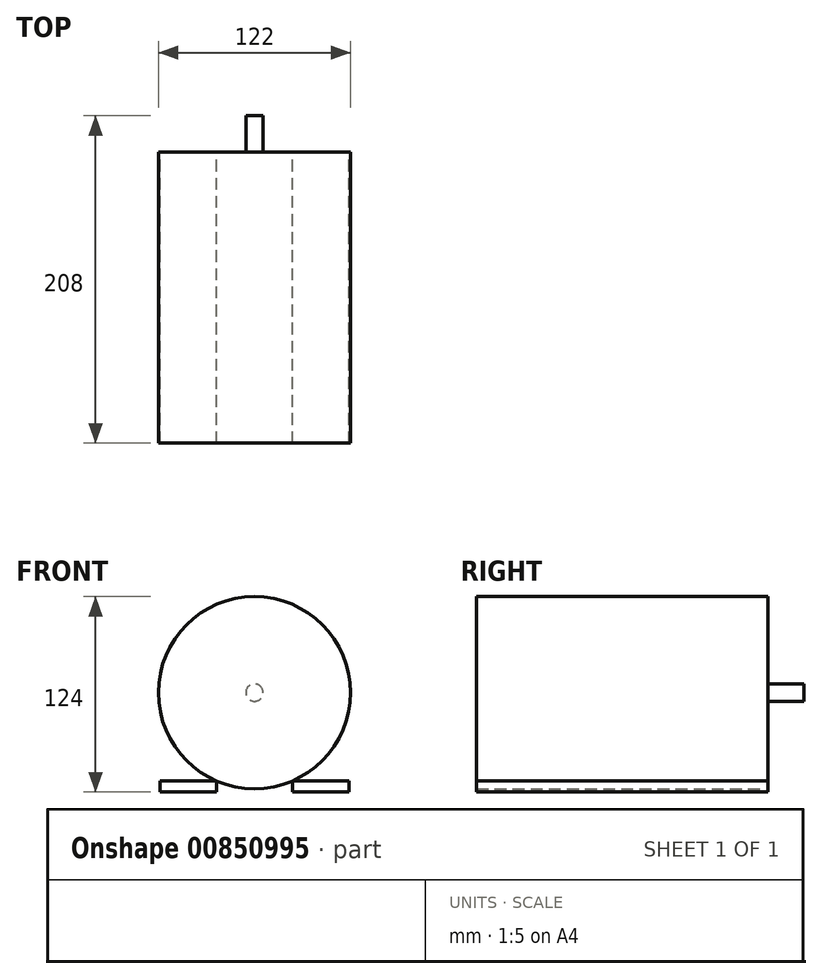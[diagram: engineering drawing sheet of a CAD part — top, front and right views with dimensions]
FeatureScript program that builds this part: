
annotation { "Feature Type Name" : "Feature", "Feature Type Description" : "" }
export const myFeature = defineFeature(function(context is Context, id is Id, definition is map)
    precondition{}
    {
        {
            var Q0;
            Q0=qCreatedBy(makeId("Front.planeOp"),FACE);
            var sketch = newSketch(context, id + "F0", { "sketchPlane" : qUnion([Q0])});
            skCircle(sketch, "E0", {"center": v(0, 0) * mm, "radius": 61 * mm});
            skLineSegment(sketch, "E1.bottom", {"start": v(-24.19, -56) * mm, "end": v(-60, -56) * mm});
            skLineSegment(sketch, "E1.top", {"start": v(-24.19, -63) * mm, "end": v(-60, -63) * mm});
            skLineSegment(sketch, "E1.left", {"start": v(-24.19, -56) * mm, "end": v(-24.19, -63) * mm});
            skLineSegment(sketch, "E1.right", {"start": v(-60, -56) * mm, "end": v(-60, -63) * mm});
            skLineSegment(sketch, "E2.bottom", {"start": v(24.19, -56) * mm, "end": v(60, -56) * mm});
            skLineSegment(sketch, "E2.top", {"start": v(24.19, -63) * mm, "end": v(60, -63) * mm});
            skLineSegment(sketch, "E2.left", {"start": v(24.19, -56) * mm, "end": v(24.19, -63) * mm});
            skLineSegment(sketch, "E2.right", {"start": v(60, -56) * mm, "end": v(60, -63) * mm});
            skSolve(sketch);
        }
        {
            var Q0;
            Q0 = qSketchRegion(id + "F0", true);
            extrude(context, id + "F1", {"entities" : qUnion([Q0]), "depth" : (208 - 23) * mm, "offsetDistance" : 25 * mm});
        }
        {
            var Q0;
            Q0=makeQuery(id+"F1.opExtrude","CAP_FACE",FACE,{"disambiguationData":[OSD([sQuery(id+"F0.wireOp",EDGE,"E0")])],"isStart":true});
            var sketch = newSketch(context, id + "F2", { "sketchPlane" : qUnion([Q0])});
            skCircle(sketch, "E3", {"center": v(0, 0) * mm, "radius": 5.5 * mm});
            skSolve(sketch);
        }
        {
            var Q0;
            Q0 = qSketchRegion(id + "F2", true);
            extrude(context, id + "F3", {"entities" : qUnion([Q0]), "operationType" : NewBodyOperationType.ADD, "depth" : 23 * mm, "offsetDistance" : 25 * mm});
        }
    });
